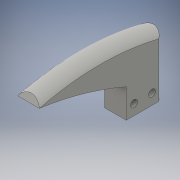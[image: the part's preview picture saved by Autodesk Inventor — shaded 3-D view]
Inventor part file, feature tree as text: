
AUTODESK INVENTOR PART (.ipt)
format: ipt  version: 2016 (Build 200138000, 138)  size: 158,720 bytes
history: native  units: in
note: dims shown in document units (in); Inventor stores cm internally (conversion verified against a paired STEP export)
features: sketch x6, extrude x3, hole x1, sweep x1
ambient origin geometry x8: Origin, YZ Plane, XZ Plane, XY Plane, X Axis, Y Axis, Z Axis, Center Point
bodies: Solid1 (feature_tree)
feature tree (11):
  extrude  "Extrusion1"  Depth=0.5in
  hole  "Hole2"  [1 undecoded]
  extrude  "Extrusion2"  Depth=0.75in TaperAngle=0.0deg
  sweep  "Sweep2"
  extrude  "Extrusion4"  Depth=1.0in
  sketch  "Sketch1"  dims[d0=0.75in d1=0.5in]
  sketch  "Sketch2"  dims[d2=0.4173in d3=0.5in d4=0.0in]
  sketch  "Sketch3"  dims[d14=0.4173in]
  sketch  "Sketch4"  dims[d15=0.1575in d16=0.75in d17=0.2362in d18=0.1181in d19=0.5635in d20=1.0in d21=0.8108in d22=0.75in d23=0.0in]
  sketch  "Sketch6"  dims[d25=0.0125in d30=0.0in d31=0.0in]
  sketch  "Sketch7"  dims[d32=0.5in d33=0.0in d5=1.0in d6=1.0in]
note: 1 required parameter value undecoded (feature->parameter linkage not recoverable at this tier; creation-order binding heuristic only, values carry confidence <= 0.55)
